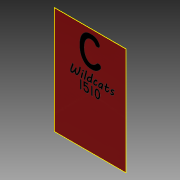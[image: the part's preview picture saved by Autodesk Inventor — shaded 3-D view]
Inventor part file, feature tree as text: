
AUTODESK INVENTOR PART (.ipt)
format: ipt  version: 2014 (Build 180170000, 170)  size: 80,384 bytes
history: native  units: in
note: dims shown in document units (in); Inventor stores cm internally (conversion verified against a paired STEP export)
features: sketch x2, extrude x1
ambient origin geometry x8: Origin, YZ Plane, XZ Plane, XY Plane, X Axis, Y Axis, Z Axis, Center Point
bodies: Solid1 (feature_tree)
feature tree (3):
  extrude  "Extrusion1"  Depth=36.0in
  sketch  "Sketch2"  dims[d2=0.01in d3=0.0in]
  sketch  "Sketch1"  dims[d0=24.0in d1=36.0in]
